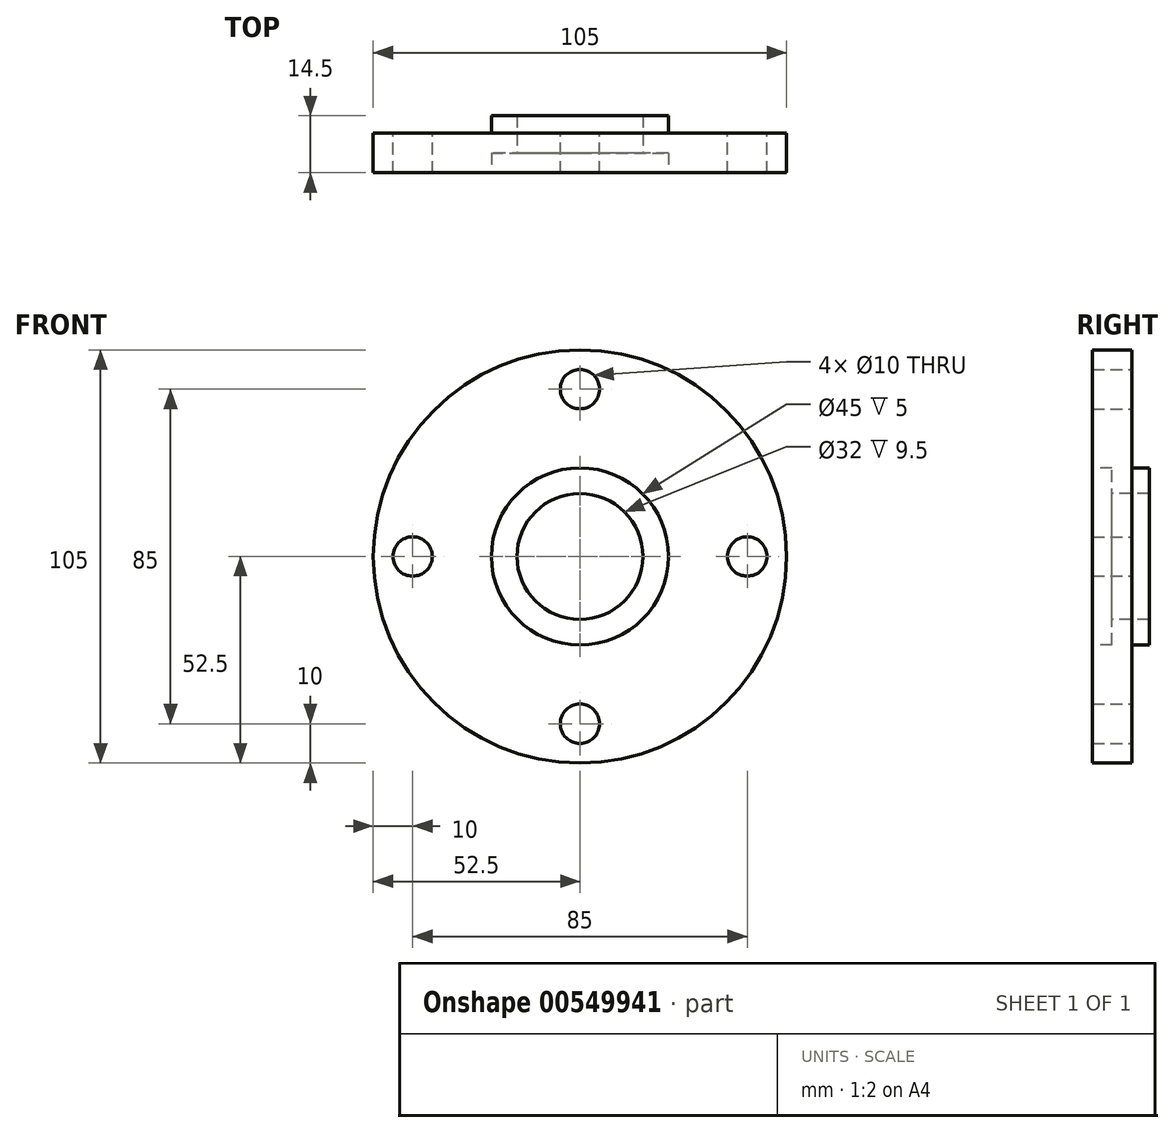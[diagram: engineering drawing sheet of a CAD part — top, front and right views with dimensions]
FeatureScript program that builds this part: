
annotation { "Feature Type Name" : "Feature", "Feature Type Description" : "" }
export const myFeature = defineFeature(function(context is Context, id is Id, definition is map)
    precondition{}
    {
        {
            var Q0;
            Q0=qCreatedBy(makeId("Front.planeOp"),FACE);
            var sketch = newSketch(context, id + "F0", { "sketchPlane" : qUnion([Q0])});
            skCircle(sketch, "E0", {"center": v(0, 0) * mm, "radius": 42.5 * mm});
            skCircle(sketch, "E1", {"center": v(0, 0) * mm, "radius": 52.5 * mm});
            skPoint(sketch, "E2", {"position": v(0, 42.5) * mm});
            skCircle(sketch, "E3", {"center": v(0, 42.5) * mm, "radius": 5 * mm});
            skCircle(sketch, "E4.1.0", {"center": v(-42.5, 0) * mm, "radius": 5 * mm});
            skCircle(sketch, "E4.2.0", {"center": v(0, -42.5) * mm, "radius": 5 * mm});
            skCircle(sketch, "E4.3.0", {"center": v(42.5, 0) * mm, "radius": 5 * mm});
            skSolve(sketch);
        }
        {
            var Q0;
            Q0 = qSketchRegion(id + "F0", true);
            var Q1;
            {var subQ1=sQuery(id+"F0.wireOp",EDGE,"E0");var subQ9=sQuery(id+"F0.wireOp",EDGE,"E3");var subQ12=makeQuery(id+"F0.imprint","INTERSECT",VERTEX,{"disambiguationData":[OD(0.0)],"derivedFrom":[subQ1,subQ9]});Q1=makeQuery(id+"F0.imprint","IMPRINT",FACE,{"disambiguationData":[TD([[makeQuery(id+"F0.imprint","IMPRINT",EDGE,{"disambiguationData":[TD([[subQ12,1.0]])],"derivedFrom":subQ1}),1.0]])]});}
            extrude(context, id + "F1", {"entities" : qUnion([Q0, Q1]), "depth" : 10 * mm, "offsetDistance" : 25 * mm});
        }
        {
            var Q0;
            Q0=makeQuery(id+"F1.opExtrude","CAP_FACE",FACE,{"disambiguationData":[OSD([sQuery(id+"F0.wireOp",EDGE,"E1"),sQuery(id+"F0.wireOp",EDGE,"E3"),sQuery(id+"F0.wireOp",EDGE,"E4.1.0"),sQuery(id+"F0.wireOp",EDGE,"E4.2.0"),sQuery(id+"F0.wireOp",EDGE,"E4.3.0")])],"isStart":false});
            var sketch = newSketch(context, id + "F2", { "sketchPlane" : qUnion([Q0])});
            skCircle(sketch, "E5", {"center": v(0, 0) * mm, "radius": 22.5 * mm});
            skCircle(sketch, "E6", {"center": v(0, 0) * mm, "radius": 16 * mm});
            skSolve(sketch);
        }
        {
            var Q0;
            Q0 = qSketchRegion(id + "F2", true);
            var Q1;
            Q1=makeQuery(id+"F2.imprint","IMPRINT",FACE,{"disambiguationData":[TD([[makeQuery(id+"F2.imprint","IMPRINT",EDGE,{"derivedFrom":sQuery(id+"F2.wireOp",EDGE,"E6")}),1.0]])]});
            extrude(context, id + "F3", {"entities" : qUnion([Q0, Q1]), "operationType" : NewBodyOperationType.REMOVE, "oppositeDirection" : true, "depth" : 5 * mm, "offsetDistance" : 25 * mm});
        }
        {
            var Q0;
            Q0=makeQuery(id+"F1.opExtrude","CAP_FACE",FACE,{"disambiguationData":[OSD([sQuery(id+"F0.wireOp",EDGE,"E1"),sQuery(id+"F0.wireOp",EDGE,"E3"),sQuery(id+"F0.wireOp",EDGE,"E4.1.0"),sQuery(id+"F0.wireOp",EDGE,"E4.2.0"),sQuery(id+"F0.wireOp",EDGE,"E4.3.0")])],"isStart":true});
            var sketch = newSketch(context, id + "F4", { "sketchPlane" : qUnion([Q0])});
            skCircle(sketch, "E7", {"center": v(0, 0) * mm, "radius": 22.5 * mm});
            skCircle(sketch, "E8", {"center": v(0, 0) * mm, "radius": 16 * mm});
            skSolve(sketch);
        }
        {
            var Q0;
            Q0 = qSketchRegion(id + "F4", true);
            extrude(context, id + "F5", {"entities" : qUnion([Q0]), "operationType" : NewBodyOperationType.ADD, "depth" : 4.5 * mm, "offsetDistance" : 25 * mm});
        }
        {
            var Q0;
            Q0=makeQuery(id+"F5.boolean.opBoolean","SPLIT",FACE,{"disambiguationData":[TD([makeQuery(id+"F5.opExtrude","SWEPT_FACE",FACE,{"disambiguationData":[OSD([sQuery(id+"F4.wireOp",EDGE,"E8")])]})])],"derivedFrom":makeQuery(id+"F1.opExtrude","CAP_FACE",FACE,{"disambiguationData":[OSD([sQuery(id+"F0.wireOp",EDGE,"E1"),sQuery(id+"F0.wireOp",EDGE,"E3"),sQuery(id+"F0.wireOp",EDGE,"E4.1.0"),sQuery(id+"F0.wireOp",EDGE,"E4.2.0"),sQuery(id+"F0.wireOp",EDGE,"E4.3.0")])],"isStart":true})});
            var sketch = newSketch(context, id + "F6", { "sketchPlane" : qUnion([Q0])});
            skCircle(sketch, "E9.0", {"center": v(0, 0) * mm, "radius": 16 * mm});
            skSolve(sketch);
        }
        {
            var Q0;
            Q0 = qSketchRegion(id + "F6", true);
            extrude(context, id + "F7", {"entities" : qUnion([Q0]), "operationType" : NewBodyOperationType.REMOVE, "oppositeDirection" : true, "depth" : 25 * mm, "offsetDistance" : 25 * mm});
        }
    });
